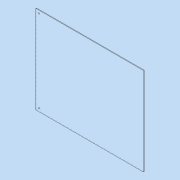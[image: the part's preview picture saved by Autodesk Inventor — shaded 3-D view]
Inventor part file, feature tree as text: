
AUTODESK INVENTOR PART (.ipt)
format: ipt  version: 2016 (Build 200138000, 138)  size: 88,576 bytes
history: native  units: mm
features: hole x2, extrude x1, sketch x1
ambient origin geometry x8: Origin, YZ Plane, XZ Plane, XY Plane, X Axis, Y Axis, Z Axis, Center Point
bodies: Solid1 (feature_tree)
feature tree (4):
  extrude  "Extrusion1"  Depth=360.0mm
  hole  "Hole1"  [1 undecoded]
  hole  "Hole2"  [1 undecoded]
  sketch  "Sketch1"  dims[d0=440.0mm d1=360.0mm d2=3.0mm d3=0.0mm d4=12.0mm d5=12.0mm d6=4.0mm d7=6.0mm d8=4.0mm d9=2.0mm d10=90.0deg d11=8.0mm d12=20.594885mm d13=12.0mm d14=12.0mm d15=4.0mm d16=6.0mm d17=4.0mm d18=2.0mm d19=90.0deg d20=8.0mm d21=20.594885mm]
note: 2 required parameter values undecoded (feature->parameter linkage not recoverable at this tier; creation-order binding heuristic only, values carry confidence <= 0.55)
